# Revit family: TD92_ALI038_AMA000_RVT20_R00
name_source: partatom
category: Mobiliário
units: mm (PartAtom-declared; Revit-internal decimal feet)

## family parameters
Com base no plano de trabalho = Não
Compartilhado = Não
Corte com vazios quando carregada = Não
Número OmniClass = 23.40.20.00
Ponto de cálculo do ambiente = Não
Sempre na vertical = Sim
Título OmniClass = General Furniture and Specialties

## types (1)
- TD92_ALI038_AMA000_RVT20_R00
    Descrição = Se você busca por uma peça para dar aquele toque que faltava na sua decoração e ambiente, você acaba de achar: Cadeira Tramontina Alice Satinada sem Braços em Polipropileno Amarelo o da linha Summa. Ela conta com um design que une linhas modernas, beleza e um acabamento em brilho, o que faz dela a escolha certa para deixar qualquer espaço ainda mais sofisticado, seja ele residencial ou empresarial. A Alice oferece cadeiras com as mais variadas cores para você compor com muita criatividade. Para manter suas características por mais tempo, além de evitar acidentes, procure não subir no assento, jogar-se sobre a cadeira ou apoiar-se somente nas pernas traseiras. Evite longa exposição ao sol. A Alice suporta uma carga estática de até 182 kg.
    Elevação padrão = 0  [stored 0 ft]
    Fabricante = Tramontina Delta S/A
    Modelo = Cadeira Tramontina Alice Satinada sem Braços em Polipropileno Amarelo
    Nota-chave = 92038000
    URL = https://www.tramontinastore.com

note: [stored X ft] marks values corroborated as IEEE doubles in the binary element streams (Revit-internal decimal feet)
